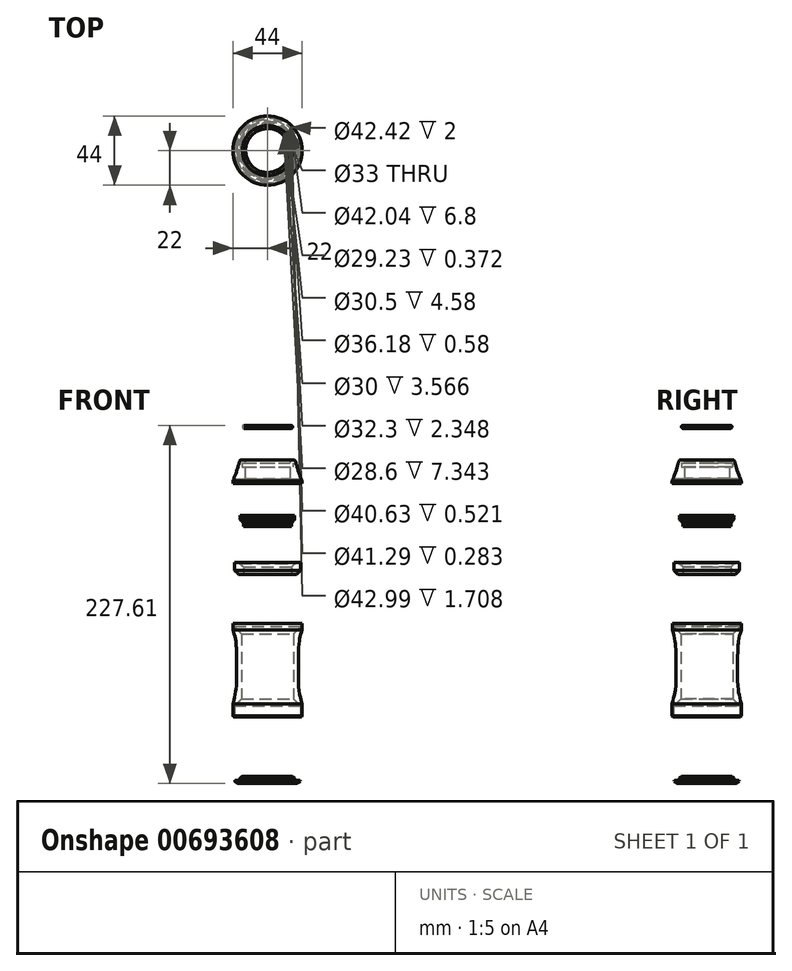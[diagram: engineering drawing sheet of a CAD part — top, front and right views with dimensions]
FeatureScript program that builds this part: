
annotation { "Feature Type Name" : "Feature", "Feature Type Description" : "" }
export const myFeature = defineFeature(function(context is Context, id is Id, definition is map)
    precondition{}
    {
        {
            var Q0;
            Q0=qCreatedBy(makeId("Front.planeOp"),FACE);
            var sketch = newSketch(context, id + "F0", { "sketchPlane" : qUnion([Q0])});
            skLineSegment(sketch, "E0", {"start": v(15.25, -7.5) * mm, "end": v(18.36, -7.5) * mm});
            skLineSegment(sketch, "E1", {"start": v(18.36, -7.5) * mm, "end": v(20.9, -4.96) * mm});
            skLineSegment(sketch, "E2", {"start": v(15.25, -7.5) * mm, "end": v(15.25, -2.92) * mm});
            skLineSegment(sketch, "E3", {"start": v(15.25, -2.92) * mm, "end": v(17.59, -0.58) * mm});
            skLineSegment(sketch, "E4", {"start": v(17.59, -0.58) * mm, "end": v(18.09, -0.58) * mm});
            skLineSegment(sketch, "E5", {"start": v(18.09, -0.58) * mm, "end": v(18.09, 0) * mm});
            skLineSegment(sketch, "E6", {"start": v(18.09, 0) * mm, "end": v(20.9, 0) * mm});
            skLineSegment(sketch, "E7", {"start": v(0, -150.83) * mm, "end": v(0, 121.4) * mm, "construction": true});
            skLineSegment(sketch, "E8", {"start": v(20.9, 0) * mm, "end": v(20.9, -4.96) * mm});
            skLineSegment(sketch, "E9", {"start": v(20.9, -4.96) * mm, "end": v(20.9, -10.27) * mm, "construction": true});
            skLineSegment(sketch, "E10", {"start": v(15.25, -2.92) * mm, "end": v(15.25, 4.24) * mm, "construction": true});
            skLineSegment(sketch, "E11", {"start": v(14.3, 29.68) * mm, "end": v(14.3, 22.99) * mm});
            skLineSegment(sketch, "E12", {"start": v(14.3, 22.99) * mm, "end": v(15.25, 22.99) * mm});
            skLineSegment(sketch, "E13", {"start": v(15.25, 22.99) * mm, "end": v(15.25, 25.21) * mm});
            skLineSegment(sketch, "E14", {"start": v(15.25, 25.21) * mm, "end": v(16.24, 26.2) * mm});
            skLineSegment(sketch, "E15", {"start": v(16.24, 26.2) * mm, "end": v(16.24, 26.68) * mm});
            skLineSegment(sketch, "E16", {"start": v(16.24, 26.68) * mm, "end": v(16.72, 26.68) * mm});
            skLineSegment(sketch, "E17", {"start": v(16.72, 26.68) * mm, "end": v(17.28, 27.24) * mm});
            skLineSegment(sketch, "E18", {"start": v(17.28, 27.24) * mm, "end": v(17.28, 28.43) * mm});
            skLineSegment(sketch, "E19", {"start": v(17.28, 28.43) * mm, "end": v(17.05, 28.43) * mm});
            skLineSegment(sketch, "E20", {"start": v(17.05, 28.43) * mm, "end": v(17.05, 28.96) * mm});
            skLineSegment(sketch, "E21", {"start": v(17.05, 28.96) * mm, "end": v(17.28, 28.96) * mm});
            skLineSegment(sketch, "E22", {"start": v(17.28, 28.96) * mm, "end": v(17.28, 30.05) * mm});
            skLineSegment(sketch, "E23", {"start": v(17.28, 30.05) * mm, "end": v(14.62, 30.05) * mm});
            skLineSegment(sketch, "E24", {"start": v(14.62, 30.05) * mm, "end": v(14.62, 29.68) * mm});
            skLineSegment(sketch, "E25", {"start": v(14.62, 29.68) * mm, "end": v(14.3, 29.68) * mm});
            skLineSegment(sketch, "E26", {"start": v(16.24, 26.2) * mm, "end": v(16.24, 25.09) * mm, "construction": true});
            skLineSegment(sketch, "E27", {"start": v(14.62, 30.05) * mm, "end": v(0, 30.05) * mm, "construction": true});
            skLineSegment(sketch, "E28", {"start": v(14.3, 65.15) * mm, "end": v(14.3, 63.16) * mm});
            skLineSegment(sketch, "E29", {"start": v(14.3, 63.16) * mm, "end": v(16.15, 63.16) * mm});
            skLineSegment(sketch, "E30", {"start": v(16.15, 63.16) * mm, "end": v(16.15, 60.81) * mm});
            skLineSegment(sketch, "E31", {"start": v(16.15, 60.81) * mm, "end": v(14.3, 60.81) * mm});
            skLineSegment(sketch, "E32", {"start": v(14.3, 60.81) * mm, "end": v(14.3, 53.47) * mm});
            skLineSegment(sketch, "E33", {"start": v(14.3, 53.47) * mm, "end": v(14.74, 53) * mm});
            skLineSegment(sketch, "E34", {"start": v(14.74, 53) * mm, "end": v(20.32, 53) * mm});
            skLineSegment(sketch, "E35", {"start": v(20.32, 53) * mm, "end": v(20.32, 52.47) * mm});
            skLineSegment(sketch, "E36", {"start": v(20.32, 52.47) * mm, "end": v(20.64, 52.47) * mm});
            skLineSegment(sketch, "E37", {"start": v(20.64, 52.47) * mm, "end": v(20.64, 52.19) * mm});
            skLineSegment(sketch, "E38", {"start": v(20.64, 52.19) * mm, "end": v(21.17, 52.19) * mm});
            skLineSegment(sketch, "E39", {"start": v(21.17, 52.19) * mm, "end": v(21.5, 51.86) * mm});
            skLineSegment(sketch, "E40", {"start": v(21.5, 51.86) * mm, "end": v(21.5, 50.15) * mm});
            skLineSegment(sketch, "E41", {"start": v(21.5, 50.15) * mm, "end": v(22, 50.15) * mm});
            skLineSegment(sketch, "E42", {"start": v(22, 50.15) * mm, "end": v(22, 51.86) * mm});
            skLineSegment(sketch, "E43", {"start": v(14.3, 65.15) * mm, "end": v(16.83, 65.15) * mm});
            skFitSpline(sketch, "E44", {"points": [v(16.83, 65.15) * mm, v(17.5, 64.84) * mm, v(18.5, 61.7) * mm, v(20.48, 55.53) * mm, v(22, 51.86) * mm], "startDerivative": vector(10.22, 0) * mm, "endDerivative": vector(4.37, -10.92) * mm});
            skLineSegment(sketch, "E45", {"start": v(21.21, -38.56) * mm, "end": v(21.21, -40.56) * mm});
            skLineSegment(sketch, "E46", {"start": v(21.21, -40.56) * mm, "end": v(16.5, -45.28) * mm});
            skLineSegment(sketch, "E47", {"start": v(16.5, -45.28) * mm, "end": v(16.5, -86.66) * mm});
            skLineSegment(sketch, "E48", {"start": v(16.5, -86.66) * mm, "end": v(21.02, -91.18) * mm});
            skLineSegment(sketch, "E49", {"start": v(21.02, -91.18) * mm, "end": v(21.02, -97.98) * mm});
            skLineSegment(sketch, "E50", {"start": v(21.02, -97.98) * mm, "end": v(21.46, -97.98) * mm});
            skLineSegment(sketch, "E51", {"start": v(21.46, -97.98) * mm, "end": v(22, -97.43) * mm});
            skLineSegment(sketch, "E52", {"start": v(22, -97.43) * mm, "end": v(22, -89.82) * mm});
            skLineSegment(sketch, "E53", {"start": v(21.21, -38.56) * mm, "end": v(21.91, -38.56) * mm});
            skLineSegment(sketch, "E54", {"start": v(21.91, -38.56) * mm, "end": v(21.91, -42.8) * mm});
            skFitSpline(sketch, "E55", {"points": [v(21.91, -42.8) * mm, v(21.08, -45.71) * mm, v(20.2, -49.76) * mm, v(19.84, -52.79) * mm, v(19.66, -56.95) * mm, v(19.62, -75.58) * mm, v(20.14, -81.95) * mm, v(21.2, -86.86) * mm, v(22, -89.82) * mm], "startDerivative": vector(-9.88, -35.47) * mm, "endDerivative": vector(10.93, -28.7) * mm});
            skLineSegment(sketch, "E56", {"start": v(16.5, -45.28) * mm, "end": v(11.05, -50.72) * mm, "construction": true});
            skLineSegment(sketch, "E57", {"start": v(16.5, -86.66) * mm, "end": v(9.67, -79.83) * mm, "construction": true});
            skLineSegment(sketch, "E58", {"start": v(15, -135.73) * mm, "end": v(15, -139.3) * mm});
            skLineSegment(sketch, "E59", {"start": v(15, -139.3) * mm, "end": v(15.92, -140.4) * mm});
            skLineSegment(sketch, "E60", {"start": v(15.92, -140.4) * mm, "end": v(18.57, -140.4) * mm});
            skLineSegment(sketch, "E61", {"start": v(18.57, -140.4) * mm, "end": v(20.87, -139.01) * mm});
            skLineSegment(sketch, "E62", {"start": v(20.87, -139.01) * mm, "end": v(20.51, -138.42) * mm});
            skLineSegment(sketch, "E63", {"start": v(20.51, -138.42) * mm, "end": v(17.3, -138.42) * mm});
            skLineSegment(sketch, "E64", {"start": v(17.3, -138.42) * mm, "end": v(17.3, -136.88) * mm});
            skLineSegment(sketch, "E65", {"start": v(17.3, -136.88) * mm, "end": v(16.02, -135.73) * mm});
            skLineSegment(sketch, "E66", {"start": v(16.02, -135.73) * mm, "end": v(15, -135.73) * mm});
            skCircle(sketch, "E67", {"center": v(15, 86.23) * mm, "radius": 1 * mm});
            skSolve(sketch);
        }
        {
            var Q0;
            Q0=makeQuery(id+"F0.imprint","IMPRINT",FACE,{"disambiguationData":[TD([[makeQuery(id+"F0.imprint","IMPRINT",EDGE,{"derivedFrom":sQuery(id+"F0.wireOp",EDGE,"E28")}),1.0]])]});
            var Q1;
            Q1=makeQuery(id+"F0.imprint","IMPRINT",FACE,{"disambiguationData":[TD([[makeQuery(id+"F0.imprint","IMPRINT",EDGE,{"derivedFrom":sQuery(id+"F0.wireOp",EDGE,"E11")}),1.0]])]});
            var Q2;
            Q2=makeQuery(id+"F0.imprint","IMPRINT",FACE,{"disambiguationData":[TD([[makeQuery(id+"F0.imprint","IMPRINT",EDGE,{"derivedFrom":sQuery(id+"F0.wireOp",EDGE,"E0")}),1.0]])]});
            var Q3;
            Q3=makeQuery(id+"F0.imprint","IMPRINT",FACE,{"disambiguationData":[TD([[makeQuery(id+"F0.imprint","IMPRINT",EDGE,{"derivedFrom":sQuery(id+"F0.wireOp",EDGE,"E45")}),1.0]])]});
            var Q4;
            Q4=makeQuery(id+"F0.imprint","IMPRINT",FACE,{"disambiguationData":[TD([[makeQuery(id+"F0.imprint","IMPRINT",EDGE,{"derivedFrom":sQuery(id+"F0.wireOp",EDGE,"E58")}),1.0]])]});
            var Q5;
            Q5=makeQuery(id+"F0.imprint","IMPRINT",FACE,{"disambiguationData":[TD([[makeQuery(id+"F0.imprint","IMPRINT",EDGE,{"derivedFrom":sQuery(id+"F0.wireOp",EDGE,"E67")}),1.0]])]});
            var Q6;
            Q6=sQuery(id+"F0.wireOp",EDGE,"E7");
            revolve(context, id + "F1", {"surfaceOperationType" : NewSurfaceOperationType.NEW, "entities" : qUnion([Q0, Q1, Q2, Q3, Q4, Q5]), "axis" : qUnion([Q6]), "revolveType" : RevolveType.FULL});
        }
    });
